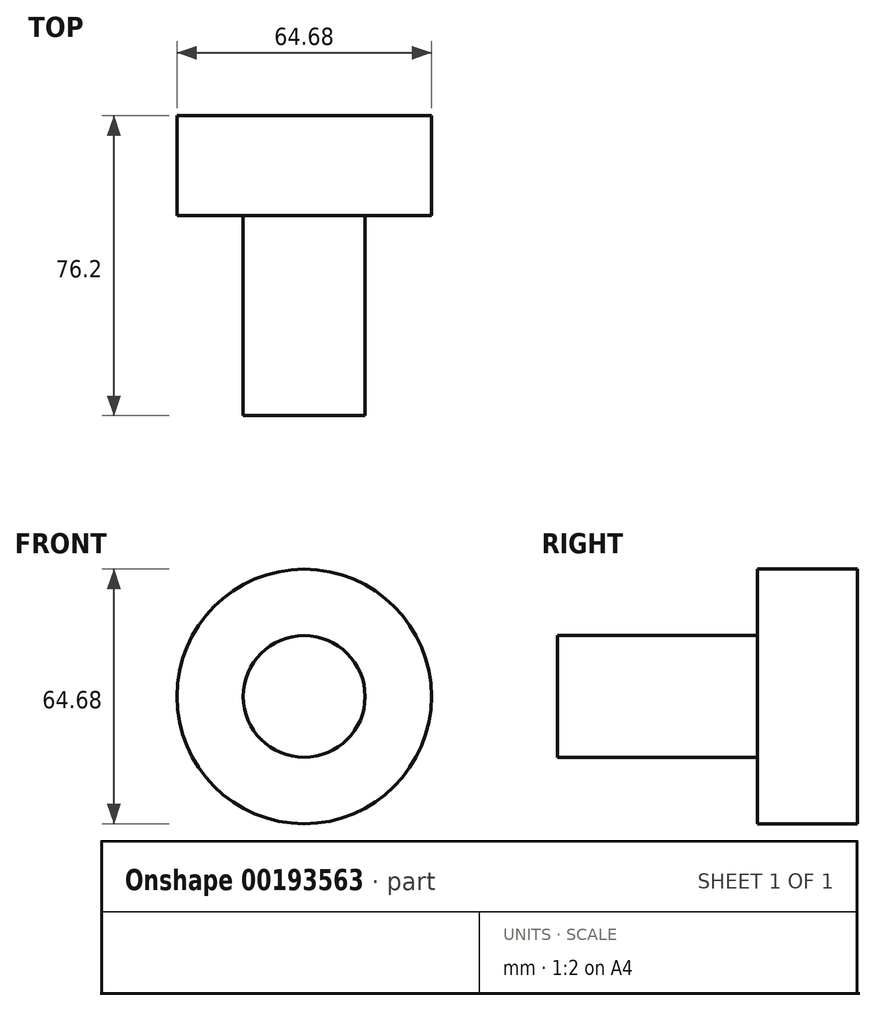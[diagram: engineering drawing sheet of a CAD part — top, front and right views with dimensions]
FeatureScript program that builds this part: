
annotation { "Feature Type Name" : "Feature", "Feature Type Description" : "" }
export const myFeature = defineFeature(function(context is Context, id is Id, definition is map)
    precondition{}
    {
        {
            var Q0;
            Q0=qCreatedBy(makeId("Front.planeOp"),FACE);
            var sketch = newSketch(context, id + "F0", { "sketchPlane" : qUnion([Q0])});
            skCircle(sketch, "E0", {"center": v(0, 0) * mm, "radius": 32.34 * mm});
            skSolve(sketch);
        }
        {
            var Q0;
            Q0=makeQuery(id+"F0.imprint","IMPRINT",FACE,{"disambiguationData":[TD([[makeQuery(id+"F0.imprint","IMPRINT",EDGE,{"derivedFrom":sQuery(id+"F0.wireOp",EDGE,"E0")}),1.0]])]});
            extrude(context, id + "F1", {"entities" : qUnion([Q0]), "depth" : 25.4 * mm});
        }
        {
            var Q0;
            Q0=qCreatedBy(makeId("Front.planeOp"),FACE);
            var sketch = newSketch(context, id + "F2", { "sketchPlane" : qUnion([Q0])});
            skCircle(sketch, "E1", {"center": v(0, 0) * mm, "radius": 15.48 * mm});
            skSolve(sketch);
        }
        {
            var Q0;
            Q0 = qSketchRegion(id + "F2", true);
            extrude(context, id + "F3", {"entities" : qUnion([Q0]), "operationType" : NewBodyOperationType.ADD, "depth" : 76.2 * mm});
        }
        {
            var Q0;
            Q0=qCreatedBy(makeId("Front.planeOp"),FACE);
            var sketch = newSketch(context, id + "F4", { "sketchPlane" : qUnion([Q0])});
            skCircle(sketch, "E2", {"center": v(0, 0) * mm, "radius": 8.1 * mm});
            skSolve(sketch);
        }
        {
            var Q0;
            Q0 = qSketchRegion(id + "F4", true);
            extrude(context, id + "F5", {"entities" : qUnion([Q0]), "operationType" : NewBodyOperationType.REMOVE, "oppositeDirection" : true, "depth" : 25.4 * mm});
        }
    });
